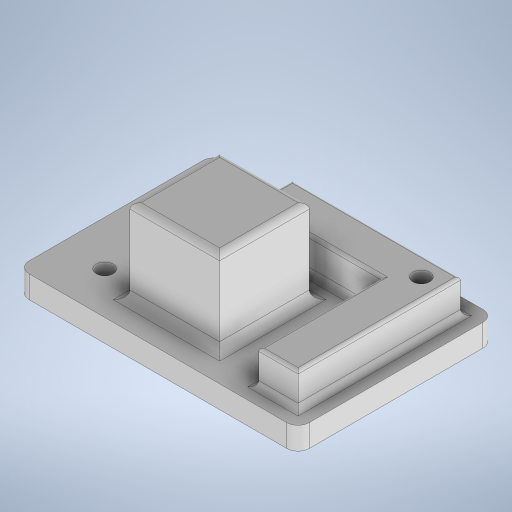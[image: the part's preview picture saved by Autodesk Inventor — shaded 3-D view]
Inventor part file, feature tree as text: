
AUTODESK INVENTOR PART (.ipt)
format: ipt  version: 2024.3 (Build 283343000, 343)  size: 351,744 bytes
history: native  units: mm
features: other x8, sketch x6, fillet x5, extrude x4, hole x2
ambient origin geometry x8: Origin, YZ Plane, XZ Plane, XY Plane, X Axis, Y Axis, Z Axis, Center Point
bodies: Solido1 (feature_tree)
feature tree (25):
  extrude  "Estrusione1"  Depth=0.5mm
  extrude  "Estrusione2"  Depth=0.35mm
  extrude  "Estrusione3"  Depth=0.04mm TaperAngle=0.0deg
  extrude  "Estrusione4"  Depth=0.03mm
  hole  "Foro1"  [1 undecoded]
  hole  "Foro2"  [1 undecoded]
  fillet  "Raccordo1"  Radius=0.3mm
  fillet  "Raccordo2"  Radius=0.06mm
  fillet  "Raccordo3"  Radius=0.03mm
  fillet  "Raccordo4"  Radius=0.07mm
  fillet  "Raccordo5"  Radius=0.06mm
  other  "Asse di lavoro3"
  sketch  "Schizzo1"
  sketch  "Schizzo2"
  other  "Linea chiusa proiettata1"
  sketch  "Schizzo3"
  other  "Linea chiusa proiettata2"
  sketch  "Schizzo4"
  other  "Linea chiusa proiettata3"
  sketch  "Schizzo5"
  other  "Linea chiusa proiettata4"
  other  "Linea chiusa proiettata5"
  other  "Linea chiusa proiettata6"
  sketch  "Schizzo6"
  other  "Linea chiusa proiettata7"
note: 2 required parameter values undecoded (feature->parameter linkage not recoverable at this tier; creation-order binding heuristic only, values carry confidence <= 0.55)
